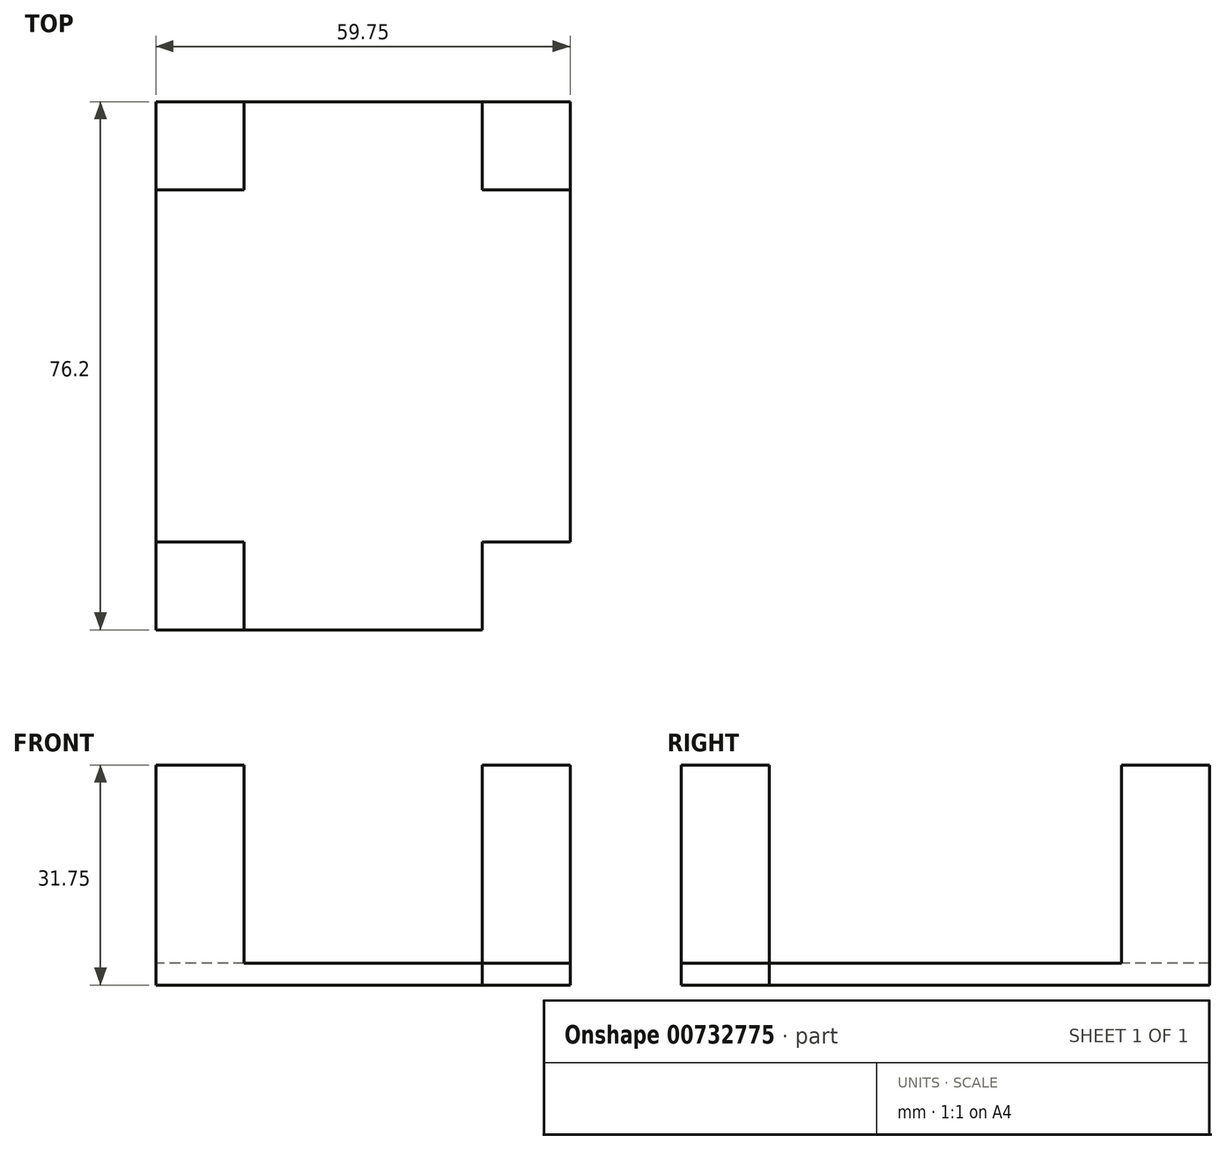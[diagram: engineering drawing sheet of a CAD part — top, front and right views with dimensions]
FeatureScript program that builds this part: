
annotation { "Feature Type Name" : "Feature", "Feature Type Description" : "" }
export const myFeature = defineFeature(function(context is Context, id is Id, definition is map)
    precondition{}
    {
        {
            var Q0;
            Q0=qCreatedBy(makeId("Top.planeOp"),FACE);
            var sketch = newSketch(context, id + "F0", { "sketchPlane" : qUnion([Q0])});
            skLineSegment(sketch, "E0", {"start": v(-36.3, -40.4) * mm, "end": v(-36.3, 35.8) * mm});
            skLineSegment(sketch, "E1.MirrorCS", {"start": v(23.46, -40.4) * mm, "end": v(23.46, 35.8) * mm});
            skLineSegment(sketch, "E2", {"start": v(-36.3, 35.8) * mm, "end": v(23.46, 35.8) * mm});
            skLineSegment(sketch, "E3", {"start": v(23.46, -40.4) * mm, "end": v(-36.3, -40.4) * mm});
            skLineSegment(sketch, "E4", {"start": v(23.46, -40.4) * mm, "end": v(23.46, -27.7) * mm});
            skLineSegment(sketch, "E5", {"start": v(23.46, -27.7) * mm, "end": v(10.76, -27.7) * mm});
            skLineSegment(sketch, "E6", {"start": v(10.76, -27.7) * mm, "end": v(10.76, -40.4) * mm});
            skLineSegment(sketch, "E7.MirrorCS", {"start": v(23.46, 23.1) * mm, "end": v(10.76, 23.1) * mm});
            skLineSegment(sketch, "E8.MirrorCS", {"start": v(10.76, 23.1) * mm, "end": v(10.76, 35.8) * mm});
            skLineSegment(sketch, "E9.MirrorCS", {"start": v(-36.3, 23.1) * mm, "end": v(-23.6, 23.1) * mm});
            skLineSegment(sketch, "E10.MirrorCS", {"start": v(-23.6, 23.1) * mm, "end": v(-23.6, 35.8) * mm});
            skLineSegment(sketch, "E11.MirrorCS", {"start": v(-36.3, -27.7) * mm, "end": v(-23.6, -27.7) * mm});
            skLineSegment(sketch, "E12.MirrorCS", {"start": v(-23.6, -27.7) * mm, "end": v(-23.6, -40.4) * mm});
            skSolve(sketch);
        }
        {
            var Q0;
            {var subQ3=sQuery(id+"F0.wireOp",EDGE,"E9.MirrorCS");Q0=makeQuery(id+"F0.imprint","IMPRINT",FACE,{"disambiguationData":[TD([[makeQuery(id+"F0.imprint","IMPRINT",EDGE,{"derivedFrom":subQ3}),1.0]])]});}
            var Q1;
            {var subQ3=sQuery(id+"F0.wireOp",EDGE,"E5");Q1=makeQuery(id+"F0.imprint","IMPRINT",FACE,{"disambiguationData":[TD([[makeQuery(id+"F0.imprint","IMPRINT",EDGE,{"derivedFrom":subQ3}),-1.0]])]});}
            var Q2;
            {var subQ3=sQuery(id+"F0.wireOp",EDGE,"E7.MirrorCS");Q2=makeQuery(id+"F0.imprint","IMPRINT",FACE,{"disambiguationData":[TD([[makeQuery(id+"F0.imprint","IMPRINT",EDGE,{"derivedFrom":subQ3}),-1.0]])]});}
            var Q3;
            {var subQ0=sQuery(id+"F0.wireOp",EDGE,"E4");Q3=makeQuery(id+"F0.imprint","IMPRINT",FACE,{"disambiguationData":[TD([[makeQuery(id+"F0.imprint","IMPRINT",EDGE,{"derivedFrom":subQ0}),1.0]])]});}
            var Q4;
            {var subQ3=sQuery(id+"F0.wireOp",EDGE,"E11.MirrorCS");Q4=makeQuery(id+"F0.imprint","IMPRINT",FACE,{"disambiguationData":[TD([[makeQuery(id+"F0.imprint","IMPRINT",EDGE,{"derivedFrom":subQ3}),-1.0]])]});}
            extrude(context, id + "F1", {"entities" : qUnion([Q0, Q1, Q2, Q3, Q4]), "depth" : 3.17 * mm, "offsetDistance" : 25.4 * mm});
        }
        {
            var Q0;
            {var subQ3=sQuery(id+"F0.wireOp",EDGE,"E9.MirrorCS");Q0=makeQuery(id+"F0.imprint","IMPRINT",FACE,{"disambiguationData":[TD([[makeQuery(id+"F0.imprint","IMPRINT",EDGE,{"derivedFrom":subQ3}),1.0]])]});}
            var Q1;
            {var subQ3=sQuery(id+"F0.wireOp",EDGE,"E7.MirrorCS");Q1=makeQuery(id+"F0.imprint","IMPRINT",FACE,{"disambiguationData":[TD([[makeQuery(id+"F0.imprint","IMPRINT",EDGE,{"derivedFrom":subQ3}),-1.0]])]});}
            var Q2;
            {var subQ3=sQuery(id+"F0.wireOp",EDGE,"E11.MirrorCS");Q2=makeQuery(id+"F0.imprint","IMPRINT",FACE,{"disambiguationData":[TD([[makeQuery(id+"F0.imprint","IMPRINT",EDGE,{"derivedFrom":subQ3}),-1.0]])]});}
            var Q3;
            {var subQ0=sQuery(id+"F0.wireOp",EDGE,"E4");Q3=makeQuery(id+"F0.imprint","IMPRINT",FACE,{"disambiguationData":[TD([[makeQuery(id+"F0.imprint","IMPRINT",EDGE,{"derivedFrom":subQ0}),1.0]])]});}
            extrude(context, id + "F2", {"entities" : qUnion([Q0, Q1, Q2, Q3]), "operationType" : NewBodyOperationType.ADD, "depth" : 31.75 * mm, "offsetDistance" : 25.4 * mm});
        }
    });
